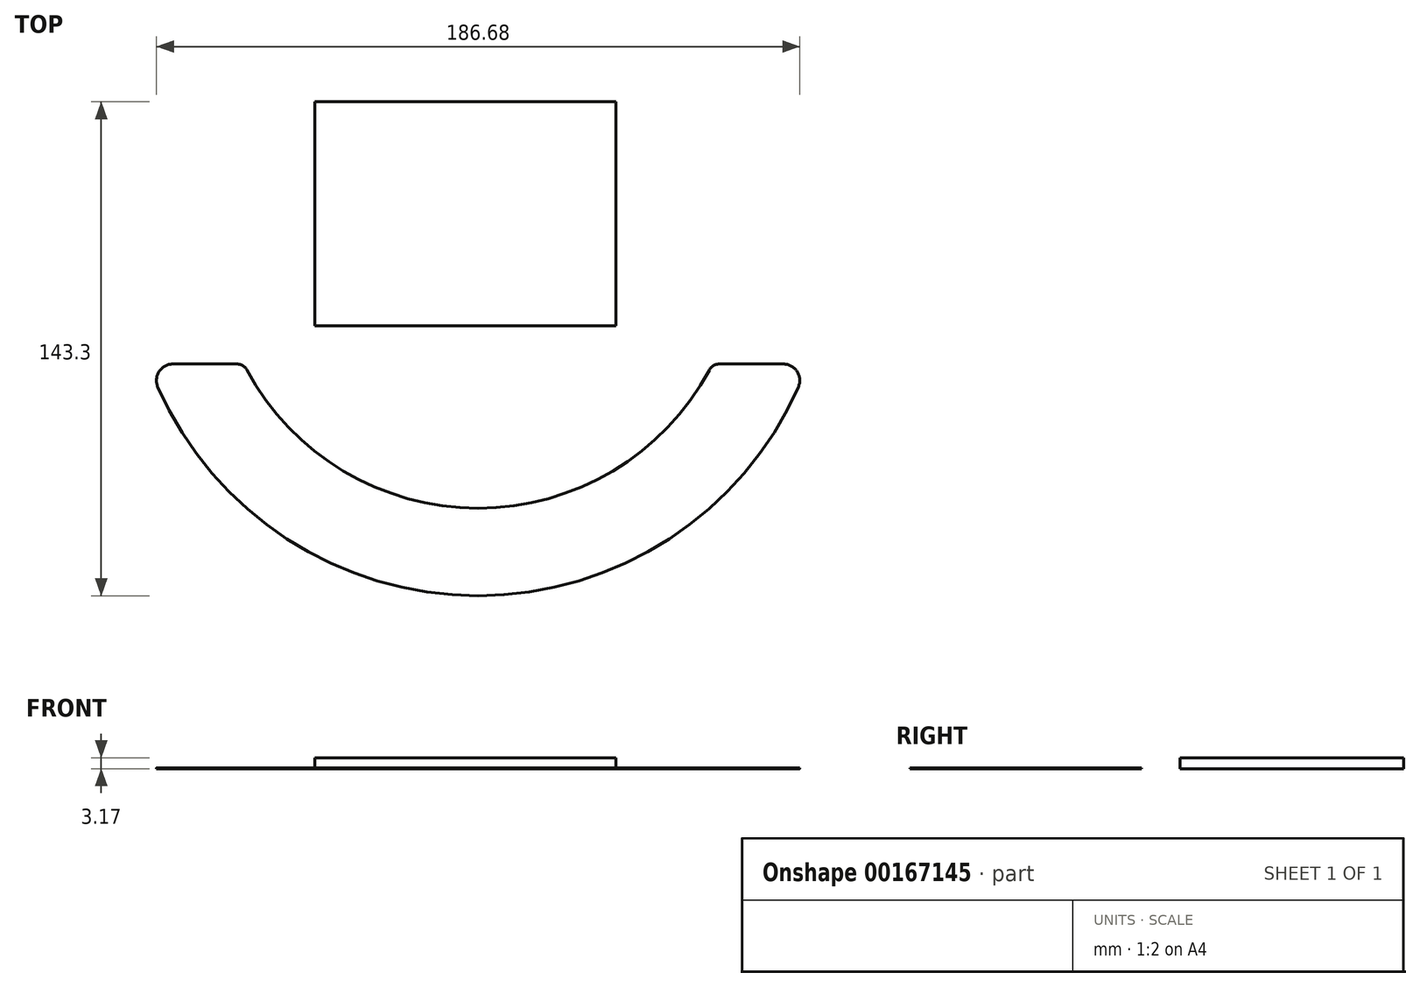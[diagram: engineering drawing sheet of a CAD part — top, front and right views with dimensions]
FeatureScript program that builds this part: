
annotation { "Feature Type Name" : "Feature", "Feature Type Description" : "" }
export const myFeature = defineFeature(function(context is Context, id is Id, definition is map)
    precondition{}
    {
        {
            var Q0;
            Q0=qCreatedBy(makeId("Top.planeOp"),FACE);
            var sketch = newSketch(context, id + "F0", { "sketchPlane" : qUnion([Q0])});
            skArc(sketch, "E0", {"start": v(-92.93, -41.06) * mm, "mid": v(0, -101.6) * mm, "end": v(92.93, -41.06) * mm});
            skArc(sketch, "E1", {"start": v(-67.13, -36.06) * mm, "mid": v(0, -76.2) * mm, "end": v(67.13, -36.06) * mm});
            skLineSegment(sketch, "E2", {"start": v(-88.59, -34.4) * mm, "end": v(-69.92, -34.4) * mm});
            skPoint(sketch, "E3.orphan", {"position": v(167.46, -34.4) * mm});
            skLineSegment(sketch, "E4", {"start": v(69.92, -34.4) * mm, "end": v(88.59, -34.4) * mm});
            skPoint(sketch, "E5.visualSharp", {"position": v(-95.6, -34.4) * mm});
            skArc(sketch, "E5.filletArc", {"start": v(-88.59, -34.4) * mm, "mid": v(-92.57, -36.55) * mm, "end": v(-92.93, -41.06) * mm});
            skPoint(sketch, "E6.visualSharp", {"position": v(95.6, -34.4) * mm});
            skArc(sketch, "E6.filletArc", {"start": v(92.93, -41.06) * mm, "mid": v(92.57, -36.55) * mm, "end": v(88.59, -34.4) * mm});
            skPoint(sketch, "E7.visualSharp", {"position": v(-68, -34.4) * mm});
            skArc(sketch, "E7.filletArc", {"start": v(-67.13, -36.06) * mm, "mid": v(-68.3, -34.84) * mm, "end": v(-69.92, -34.4) * mm});
            skPoint(sketch, "E8.visualSharp", {"position": v(68, -34.4) * mm});
            skArc(sketch, "E8.filletArc", {"start": v(69.92, -34.4) * mm, "mid": v(68.3, -34.84) * mm, "end": v(67.13, -36.06) * mm});
            skSolve(sketch);
        }
        {
            var Q0;
            Q0=makeQuery(id+"F0.imprint","IMPRINT",FACE,{"disambiguationData":[TD([[makeQuery(id+"F0.imprint","IMPRINT",EDGE,{"derivedFrom":sQuery(id+"F0.wireOp",EDGE,"E0")}),1.0]])]});
            extrude(context, id + "F1", {"entities" : qUnion([Q0]), "offsetDistance" : 25.4 * mm, "depth" : 0.25 * mm});
        }
        {
            var Q0;
            Q0=qCreatedBy(makeId("Top.planeOp"),FACE);
            var sketch = newSketch(context, id + "F2", { "sketchPlane" : qUnion([Q0])});
            skLineSegment(sketch, "E9.bottom", {"start": v(-47.34, -23.29) * mm, "end": v(40.03, -23.29) * mm});
            skLineSegment(sketch, "E9.top", {"start": v(-47.34, 41.7) * mm, "end": v(40.03, 41.7) * mm});
            skLineSegment(sketch, "E9.left", {"start": v(-47.34, -23.29) * mm, "end": v(-47.34, 41.7) * mm});
            skLineSegment(sketch, "E9.right", {"start": v(40.03, -23.29) * mm, "end": v(40.03, 41.7) * mm});
            skSolve(sketch);
        }
        {
            var Q0;
            Q0=makeQuery(id+"F2.imprint","IMPRINT",FACE,{"disambiguationData":[TD([[makeQuery(id+"F2.imprint","IMPRINT",EDGE,{"derivedFrom":sQuery(id+"F2.wireOp",EDGE,"E9.bottom")}),1.0]])]});
            extrude(context, id + "F3", {"entities" : qUnion([Q0]), "depth" : 3.17 * mm, "offsetDistance" : 25.4 * mm});
        }
    });
